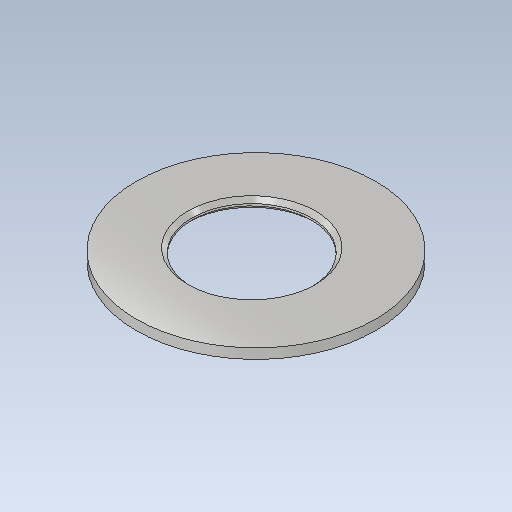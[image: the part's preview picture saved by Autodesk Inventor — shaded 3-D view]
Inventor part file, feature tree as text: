
AUTODESK INVENTOR PART (.ipt)
format: ipt  version: 2020.1 (Build 241239000, 239)  size: 109,568 bytes
history: native  units: mm
features: extrude x1, chamfer x1, sketch x1
ambient origin geometry x8: Origin, YZ Plane, XZ Plane, XY Plane, X Axis, Y Axis, Z Axis, Center Point
bodies: Solid1 (feature_tree)
feature tree (3):
  extrude  "Extrusion1"  Depth=0.5mm
  chamfer  "Chamfer1"  Distance=0.5mm
  sketch  "Sketch1"  dims[d0=6.0mm d1=12.0mm d2=0.5mm d3=0.0mm d4=0.2mm d5=2.0mm d6=45.0deg]
